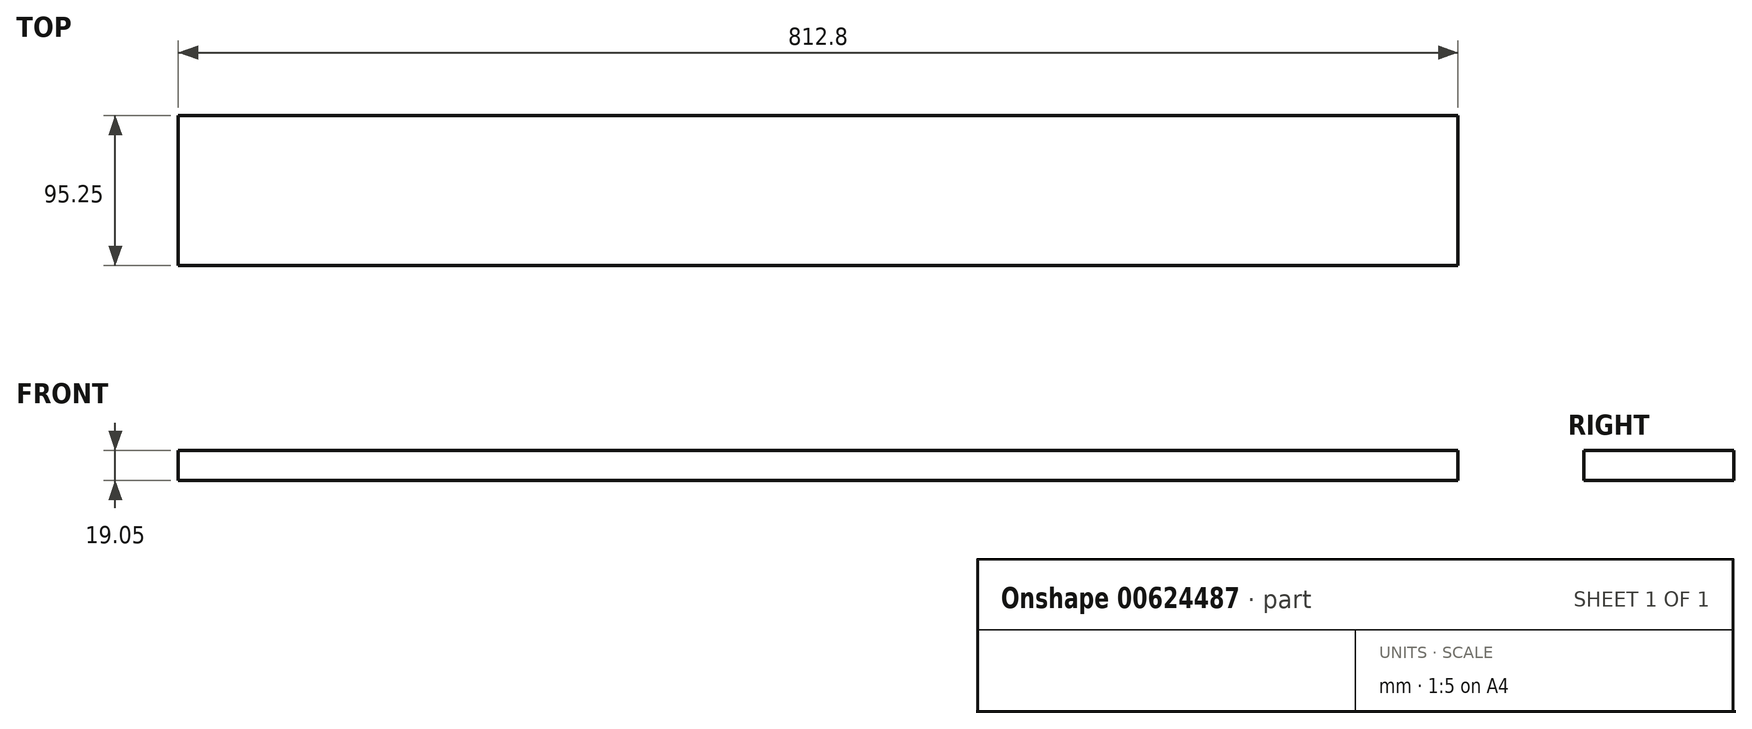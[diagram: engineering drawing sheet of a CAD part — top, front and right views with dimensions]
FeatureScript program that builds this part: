
annotation { "Feature Type Name" : "Feature", "Feature Type Description" : "" }
export const myFeature = defineFeature(function(context is Context, id is Id, definition is map)
    precondition{}
    {
        {
            var Q0;
            Q0=qCreatedBy(makeId("Top.planeOp"),FACE);
            var sketch = newSketch(context, id + "F0", { "sketchPlane" : qUnion([Q0])});
            skLineSegment(sketch, "E0.bottom", {"start": v(0, 0) * mm, "end": v(812.8, 0) * mm});
            skLineSegment(sketch, "E0.top", {"start": v(0, 95.25) * mm, "end": v(812.8, 95.25) * mm});
            skLineSegment(sketch, "E0.left", {"start": v(0, 0) * mm, "end": v(0, 95.25) * mm});
            skLineSegment(sketch, "E0.right", {"start": v(812.8, 0) * mm, "end": v(812.8, 95.25) * mm});
            skSolve(sketch);
        }
        {
            var Q0;
            Q0=makeQuery(id+"F0.imprint","IMPRINT",FACE,{"disambiguationData":[TD([[makeQuery(id+"F0.imprint","IMPRINT",EDGE,{"derivedFrom":sQuery(id+"F0.wireOp",EDGE,"E0.bottom")}),1.0]])]});
            extrude(context, id + "F1", {"entities" : qUnion([Q0]), "depth" : 19.05 * mm, "offsetDistance" : 25.4 * mm});
        }
    });
